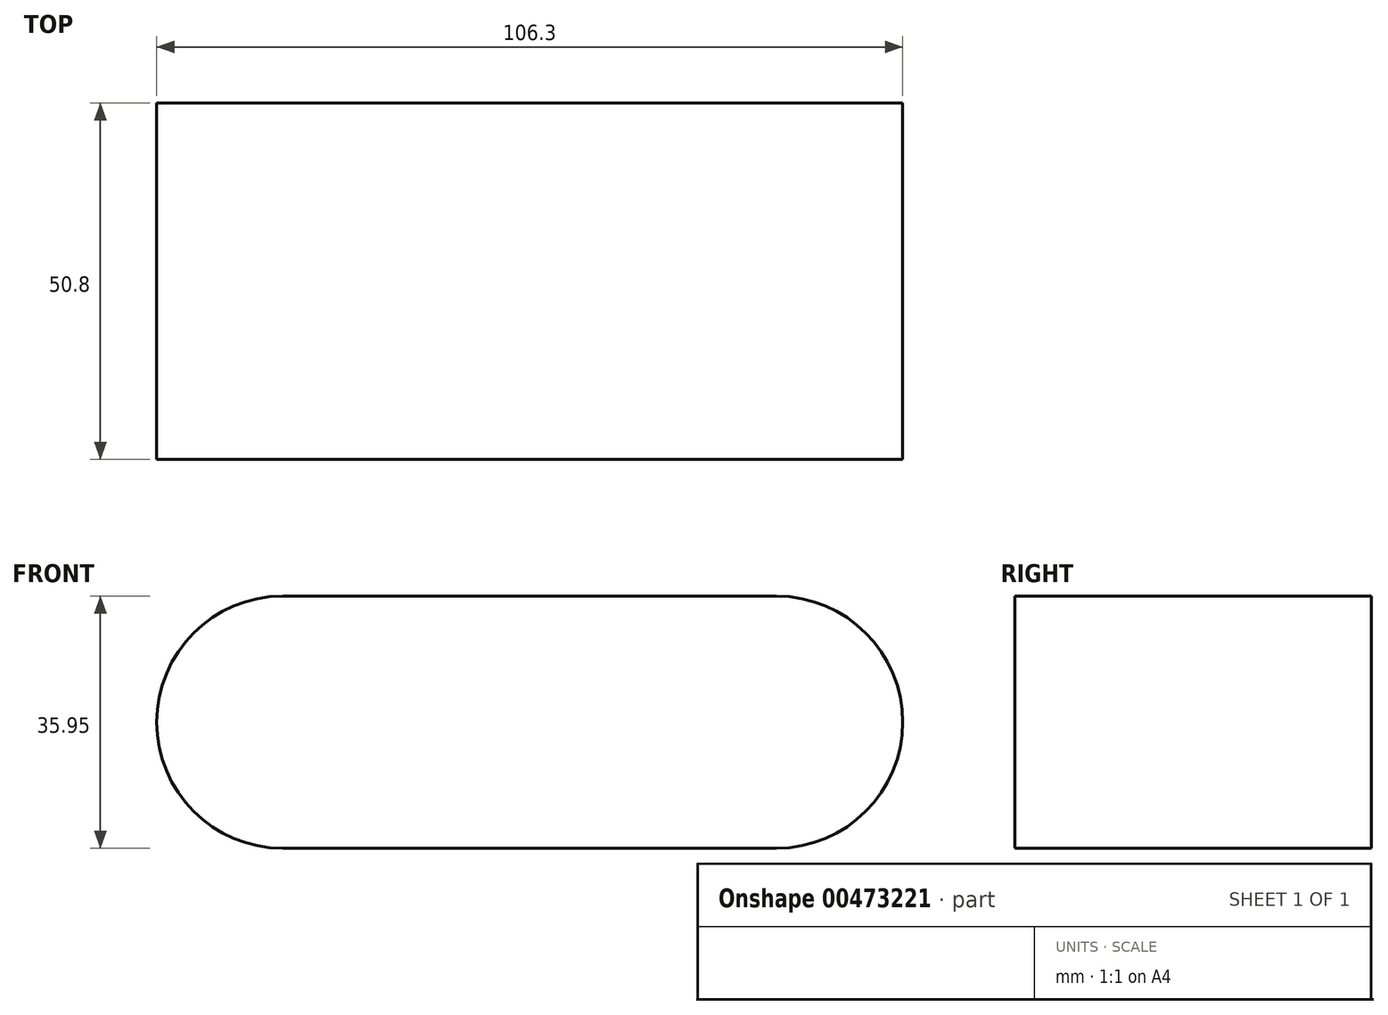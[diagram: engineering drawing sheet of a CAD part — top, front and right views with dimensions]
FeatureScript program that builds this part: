
annotation { "Feature Type Name" : "Feature", "Feature Type Description" : "" }
export const myFeature = defineFeature(function(context is Context, id is Id, definition is map)
    precondition{}
    {
        {
            var Q0;
            Q0=qCreatedBy(makeId("Front.planeOp"),FACE);
            var sketch = newSketch(context, id + "F0", { "sketchPlane" : qUnion([Q0])});
            skArc(sketch, "E0", {"start": v(-43.93, 30.68) * mm, "mid": v(-61.9, 12.7) * mm, "end": v(-43.93, -5.27) * mm});
            skArc(sketch, "E1", {"start": v(26.42, -5.27) * mm, "mid": v(44.4, 12.7) * mm, "end": v(26.42, 30.68) * mm});
            skLineSegment(sketch, "E2", {"start": v(-43.93, 30.68) * mm, "end": v(26.42, 30.68) * mm});
            skLineSegment(sketch, "E3", {"start": v(-43.93, -5.27) * mm, "end": v(26.42, -5.27) * mm});
            skSolve(sketch);
        }
        {
            var Q0;
            Q0 = qSketchRegion(id + "F0", true);
            extrude(context, id + "F1", {"entities" : qUnion([Q0]), "depth" : 25.4 * mm, "hasSecondDirection" : true, "secondDirectionOppositeDirection" : true, "secondDirectionDepth" : 25.4 * mm});
        }
    });
